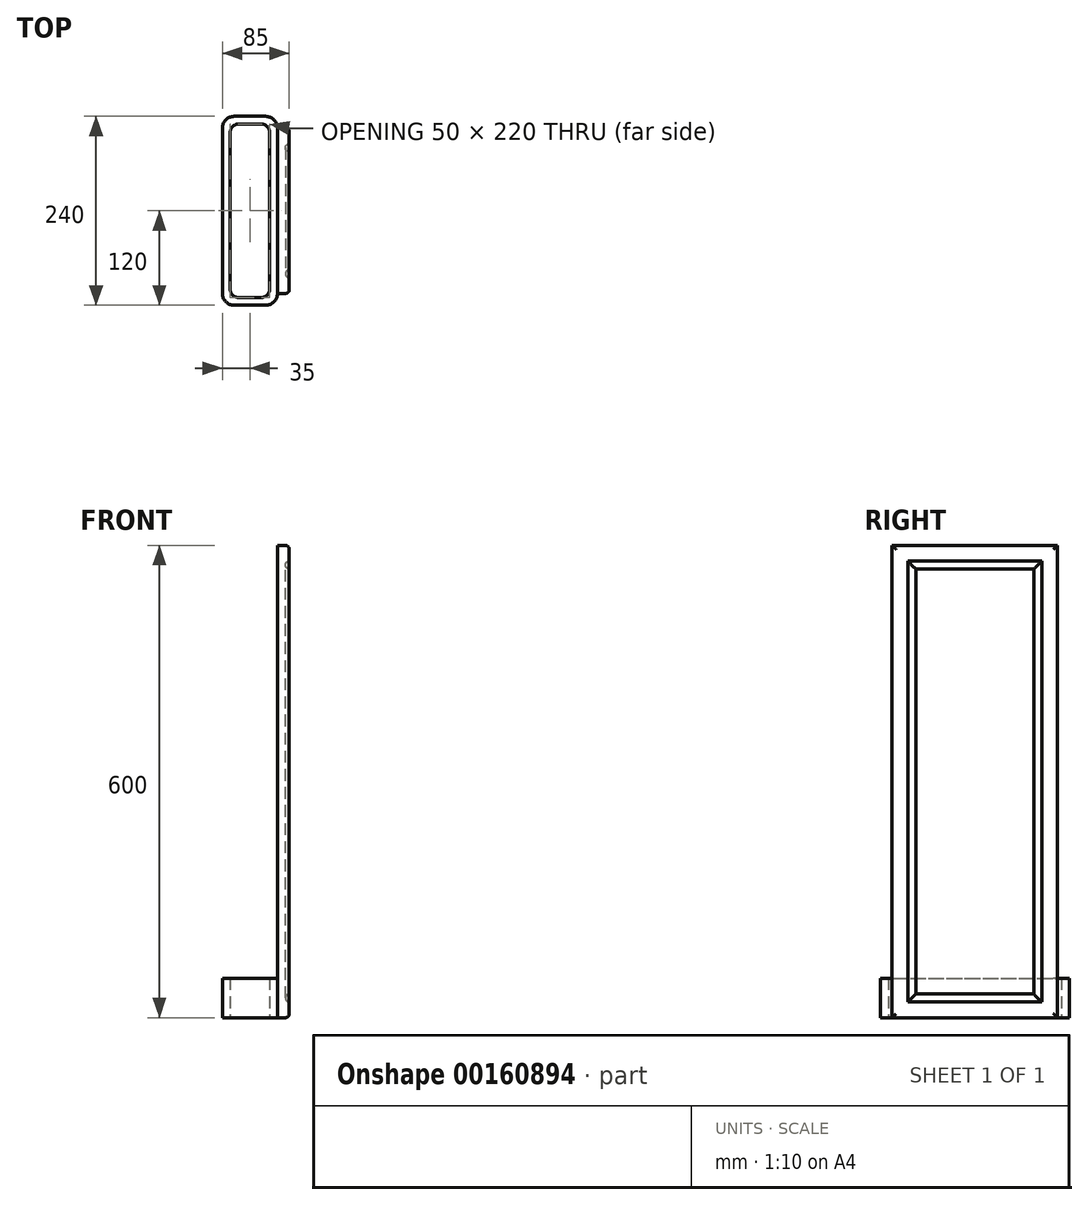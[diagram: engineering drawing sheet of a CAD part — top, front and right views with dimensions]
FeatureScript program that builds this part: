
annotation { "Feature Type Name" : "Feature", "Feature Type Description" : "" }
export const myFeature = defineFeature(function(context is Context, id is Id, definition is map)
    precondition{}
    {
        {
            var Q0;
            Q0=qCreatedBy(makeId("Top.planeOp"),FACE);
            var sketch = newSketch(context, id + "F0", { "sketchPlane" : qUnion([Q0])});
            skLineSegment(sketch, "E0.bottom", {"start": v(0, 0) * mm, "end": v(-70, 0) * mm});
            skLineSegment(sketch, "E0.top", {"start": v(0, 240) * mm, "end": v(-70, 240) * mm});
            skLineSegment(sketch, "E0.left", {"start": v(0, 0) * mm, "end": v(0, 240) * mm});
            skLineSegment(sketch, "E0.right", {"start": v(-70, 0) * mm, "end": v(-70, 240) * mm});
            skLineSegment(sketch, "E1.0", {"start": v(-10, 10) * mm, "end": v(-60, 10) * mm});
            skLineSegment(sketch, "E1.1", {"start": v(-10, 10) * mm, "end": v(-10, 230) * mm});
            skLineSegment(sketch, "E1.2", {"start": v(-10, 230) * mm, "end": v(-60, 230) * mm});
            skLineSegment(sketch, "E1.3", {"start": v(-60, 10) * mm, "end": v(-60, 230) * mm});
            skSolve(sketch);
        }
        {
            var Q0;
            Q0=makeQuery(id+"F0.imprint","IMPRINT",FACE,{"disambiguationData":[TD([[makeQuery(id+"F0.imprint","IMPRINT",EDGE,{"derivedFrom":sQuery(id+"F0.wireOp",EDGE,"E0.bottom")}),-1.0]])]});
            extrude(context, id + "F1", {"entities" : qUnion([Q0]), "depth" : 50 * mm});
        }
        {
            var Q0;
            Q0=makeQuery(id+"F1.opExtrude","SWEPT_EDGE",EDGE,{"disambiguationData":[OSD([sQuery(id+"F0.wireOp",EDGE,"E0.bottom"),sQuery(id+"F0.wireOp",EDGE,"E0.right")])]});
            var Q1;
            Q1=makeQuery(id+"F1.opExtrude","SWEPT_EDGE",EDGE,{"disambiguationData":[OSD([sQuery(id+"F0.wireOp",EDGE,"E0.bottom"),sQuery(id+"F0.wireOp",EDGE,"E0.left")])]});
            var Q2;
            Q2=makeQuery(id+"F1.opExtrude","SWEPT_EDGE",EDGE,{"disambiguationData":[OSD([sQuery(id+"F0.wireOp",EDGE,"E0.top"),sQuery(id+"F0.wireOp",EDGE,"E0.right")])]});
            var Q3;
            Q3=makeQuery(id+"F1.opExtrude","SWEPT_EDGE",EDGE,{"disambiguationData":[OSD([sQuery(id+"F0.wireOp",EDGE,"E0.top"),sQuery(id+"F0.wireOp",EDGE,"E0.left")])]});
            fillet(context, id + "F2", {"entities" : qUnion([Q0, Q1, Q2, Q3]), "radius" : 15 * mm, "tangentPropagation" : true, "allowEdgeOverflow" : false});
        }
        {
            var Q0;
            Q0=makeQuery(id+"F1.opExtrude","SWEPT_EDGE",EDGE,{"disambiguationData":[OSD([sQuery(id+"F0.wireOp",EDGE,"E1.0"),sQuery(id+"F0.wireOp",EDGE,"E1.1")])]});
            var Q1;
            Q1=makeQuery(id+"F1.opExtrude","SWEPT_EDGE",EDGE,{"disambiguationData":[OSD([sQuery(id+"F0.wireOp",EDGE,"E1.0"),sQuery(id+"F0.wireOp",EDGE,"E1.3")])]});
            var Q2;
            Q2=makeQuery(id+"F1.opExtrude","SWEPT_EDGE",EDGE,{"disambiguationData":[OSD([sQuery(id+"F0.wireOp",EDGE,"E1.1"),sQuery(id+"F0.wireOp",EDGE,"E1.2")])]});
            var Q3;
            Q3=makeQuery(id+"F1.opExtrude","SWEPT_EDGE",EDGE,{"disambiguationData":[OSD([sQuery(id+"F0.wireOp",EDGE,"E1.2"),sQuery(id+"F0.wireOp",EDGE,"E1.3")])]});
            fillet(context, id + "F3", {"entities" : qUnion([Q0, Q1, Q2, Q3]), "radius" : 10 * mm, "tangentPropagation" : true, "allowEdgeOverflow" : false});
        }
        {
            var Q0;
            Q0=makeQuery(id+"F1.opExtrude","SWEPT_FACE",FACE,{"disambiguationData":[OSD([sQuery(id+"F0.wireOp",EDGE,"E0.left")])]});
            var sketch = newSketch(context, id + "F4", { "sketchPlane" : qUnion([Q0])});
            skLineSegment(sketch, "E2.bottom", {"start": v(15, 0) * mm, "end": v(225, 0) * mm});
            skLineSegment(sketch, "E2.top", {"start": v(15, 600) * mm, "end": v(225, 600) * mm});
            skLineSegment(sketch, "E2.left", {"start": v(15, 0) * mm, "end": v(15, 600) * mm});
            skLineSegment(sketch, "E2.right", {"start": v(225, 0) * mm, "end": v(225, 600) * mm});
            skSolve(sketch);
        }
        {
            var Q0;
            {var subQ0=sQuery(id+"F4.wireOp",EDGE,"E2.bottom");Q0=makeQuery(id+"F4.imprint","IMPRINT",FACE,{"disambiguationData":[TD([[makeQuery(id+"F4.imprint","IMPRINT",EDGE,{"derivedFrom":subQ0}),1.0]])]});}
            var Q1;
            {var subQ0=sQuery(id+"F4.wireOp",EDGE,"E2.bottom");Q1=makeQuery(id+"F4.imprint","IMPRINT",FACE,{"disambiguationData":[TD([[makeQuery(id+"F4.imprint","IMPRINT",EDGE,{"derivedFrom":subQ0}),1.0]])]});}
            var Q2;
            {var subQ0=sQuery(id+"F4.wireOp",EDGE,"E2.top");Q2=makeQuery(id+"F4.imprint","IMPRINT",FACE,{"disambiguationData":[TD([[makeQuery(id+"F4.imprint","IMPRINT",EDGE,{"derivedFrom":subQ0}),-1.0]])]});}
            extrude(context, id + "F5", {"entities" : qUnion([Q0, Q1, Q2]), "depth" : 15 * mm});
        }
        {
            var Q0;
            Q0=makeQuery(id+"F5.opExtrude","CAP_FACE",FACE,{"disambiguationData":[OSD([sQuery(id+"F4.wireOp",EDGE,"E2.bottom"),sQuery(id+"F4.wireOp",EDGE,"E2.top"),sQuery(id+"F4.wireOp",EDGE,"E2.left"),sQuery(id+"F4.wireOp",EDGE,"E2.right")])],"isStart":false});
            var sketch = newSketch(context, id + "F6", { "sketchPlane" : qUnion([Q0])});
            skLineSegment(sketch, "E3.0", {"start": v(35, 20) * mm, "end": v(205, 20) * mm});
            skLineSegment(sketch, "E3.1", {"start": v(35, 580) * mm, "end": v(35, 20) * mm});
            skLineSegment(sketch, "E3.2", {"start": v(35, 580) * mm, "end": v(205, 580) * mm});
            skLineSegment(sketch, "E3.3", {"start": v(205, 20) * mm, "end": v(205, 580) * mm});
            skLineSegment(sketch, "E4.0", {"start": v(45, 30) * mm, "end": v(195, 30) * mm});
            skLineSegment(sketch, "E4.1", {"start": v(45, 570) * mm, "end": v(45, 30) * mm});
            skLineSegment(sketch, "E4.2", {"start": v(45, 570) * mm, "end": v(195, 570) * mm});
            skLineSegment(sketch, "E4.3", {"start": v(195, 30) * mm, "end": v(195, 570) * mm});
            skSolve(sketch);
        }
        {
            var Q0;
            Q0=makeQuery(id+"F6.imprint","IMPRINT",FACE,{"disambiguationData":[TD([[makeQuery(id+"F6.imprint","IMPRINT",EDGE,{"derivedFrom":sQuery(id+"F6.wireOp",EDGE,"E3.0")}),1.0]])]});
            extrude(context, id + "F7", {"entities" : qUnion([Q0]), "operationType" : NewBodyOperationType.REMOVE, "oppositeDirection" : true, "depth" : 5 * mm});
        }
        {
            var Q0;
            Q0=makeQuery(id+"F7.boolean.opBoolean","COPY",EDGE,{"derivedFrom":makeQuery(id+"F7.opExtrude","CAP_EDGE",EDGE,{"disambiguationData":[OSD([sQuery(id+"F6.wireOp",EDGE,"E3.0")])],"isStart":false})});
            var Q1;
            Q1=makeQuery(id+"F7.boolean.opBoolean","COPY",EDGE,{"derivedFrom":makeQuery(id+"F7.opExtrude","CAP_EDGE",EDGE,{"disambiguationData":[OSD([sQuery(id+"F6.wireOp",EDGE,"E4.0")])],"isStart":false})});
            var Q2;
            Q2=makeQuery(id+"F7.boolean.opBoolean","COPY",EDGE,{"derivedFrom":makeQuery(id+"F7.opExtrude","CAP_EDGE",EDGE,{"disambiguationData":[OSD([sQuery(id+"F6.wireOp",EDGE,"E3.1")])],"isStart":false})});
            var Q3;
            Q3=makeQuery(id+"F7.boolean.opBoolean","COPY",EDGE,{"derivedFrom":makeQuery(id+"F7.opExtrude","CAP_EDGE",EDGE,{"disambiguationData":[OSD([sQuery(id+"F6.wireOp",EDGE,"E3.2")])],"isStart":false})});
            var Q4;
            Q4=makeQuery(id+"F7.boolean.opBoolean","COPY",EDGE,{"derivedFrom":makeQuery(id+"F7.opExtrude","CAP_EDGE",EDGE,{"disambiguationData":[OSD([sQuery(id+"F6.wireOp",EDGE,"E4.3")])],"isStart":false})});
            var Q5;
            Q5=makeQuery(id+"F7.boolean.opBoolean","COPY",EDGE,{"derivedFrom":makeQuery(id+"F7.opExtrude","CAP_EDGE",EDGE,{"disambiguationData":[OSD([sQuery(id+"F6.wireOp",EDGE,"E4.1")])],"isStart":false})});
            var Q6;
            Q6=makeQuery(id+"F7.boolean.opBoolean","COPY",EDGE,{"derivedFrom":makeQuery(id+"F7.opExtrude","CAP_EDGE",EDGE,{"disambiguationData":[OSD([sQuery(id+"F6.wireOp",EDGE,"E4.2")])],"isStart":false})});
            var Q7;
            Q7=makeQuery(id+"F7.boolean.opBoolean","COPY",EDGE,{"derivedFrom":makeQuery(id+"F7.opExtrude","CAP_EDGE",EDGE,{"disambiguationData":[OSD([sQuery(id+"F6.wireOp",EDGE,"E3.3")])],"isStart":false})});
            fillet(context, id + "F8", {"entities" : qUnion([Q0, Q1, Q2, Q3, Q4, Q5, Q6, Q7]), "radius" : 5 * mm, "tangentPropagation" : true, "allowEdgeOverflow" : false});
        }
        {
            var Q0;
            Q0=makeQuery(id+"F5.opExtrude","CAP_EDGE",EDGE,{"disambiguationData":[OSD([sQuery(id+"F4.wireOp",EDGE,"E2.bottom")])],"isStart":false});
            var Q1;
            Q1=makeQuery(id+"F5.opExtrude","CAP_EDGE",EDGE,{"disambiguationData":[OSD([sQuery(id+"F4.wireOp",EDGE,"E2.right")])],"isStart":false});
            var Q2;
            Q2=makeQuery(id+"F5.opExtrude","CAP_EDGE",EDGE,{"disambiguationData":[OSD([sQuery(id+"F4.wireOp",EDGE,"E2.left")])],"isStart":false});
            var Q3;
            Q3=makeQuery(id+"F5.opExtrude","CAP_EDGE",EDGE,{"disambiguationData":[OSD([sQuery(id+"F4.wireOp",EDGE,"E2.top")])],"isStart":false});
            fillet(context, id + "F9", {"entities" : qUnion([Q0, Q1, Q2, Q3]), "radius" : 5 * mm, "tangentPropagation" : true, "allowEdgeOverflow" : false});
        }
    });
